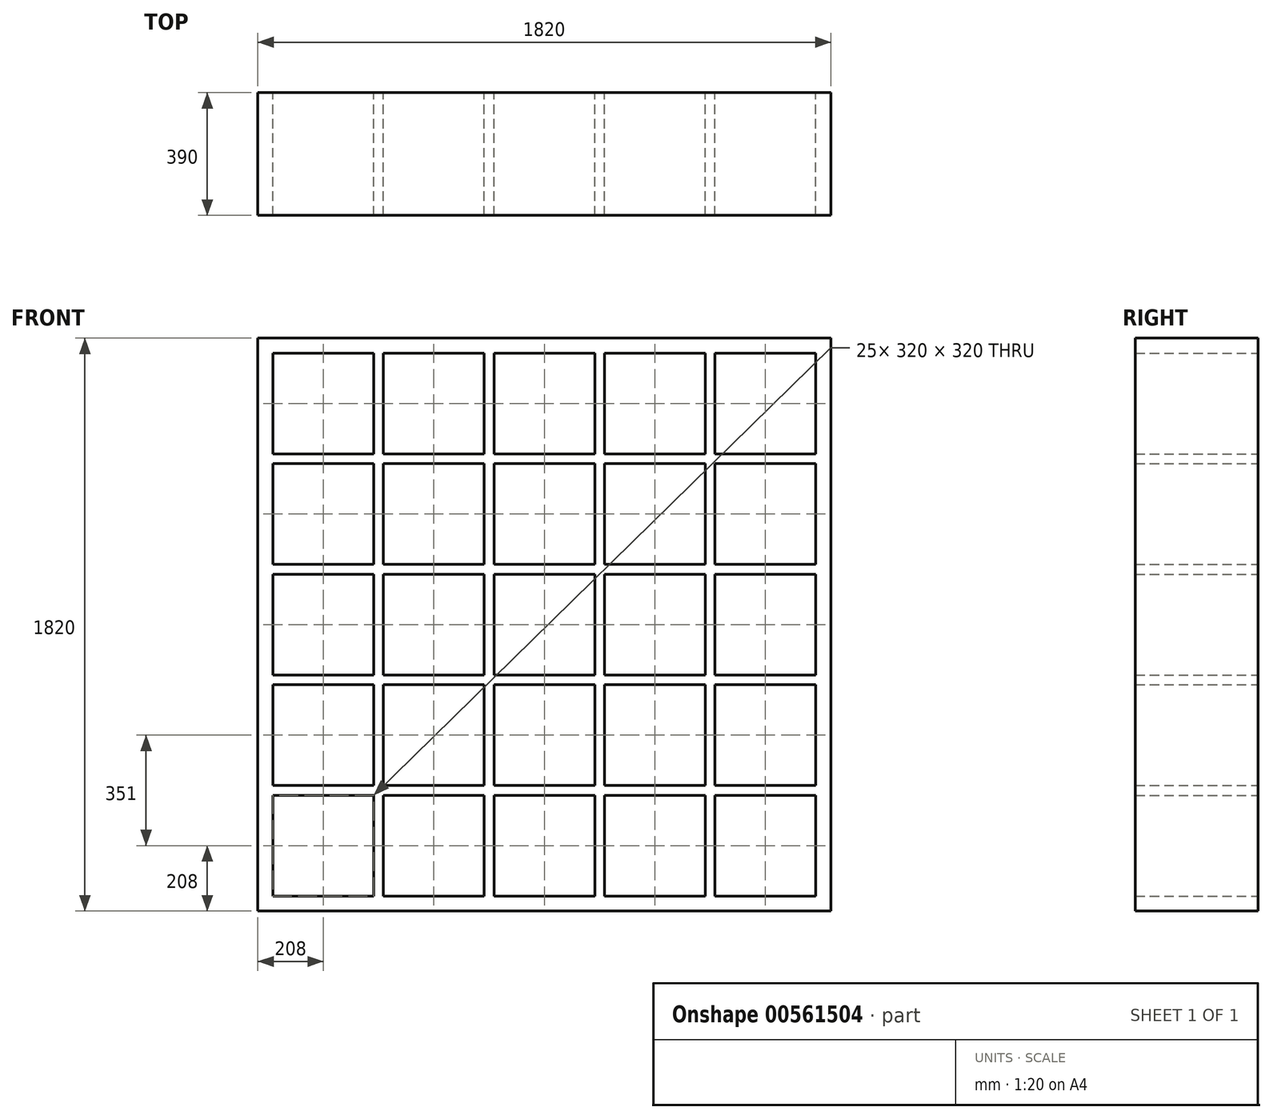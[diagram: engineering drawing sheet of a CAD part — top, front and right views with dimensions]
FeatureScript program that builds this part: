
annotation { "Feature Type Name" : "Feature", "Feature Type Description" : "" }
export const myFeature = defineFeature(function(context is Context, id is Id, definition is map)
    precondition{}
    {
        {
            var Q0;
            Q0=qCreatedBy(makeId("Front.planeOp"),FACE);
            var sketch = newSketch(context, id + "F0", { "sketchPlane" : qUnion([Q0])});
            skLineSegment(sketch, "E0.bottom", {"start": v(0, 0) * mm, "end": v(1820, 0) * mm});
            skLineSegment(sketch, "E0.top", {"start": v(0, 1820) * mm, "end": v(1820, 1820) * mm});
            skLineSegment(sketch, "E0.left", {"start": v(0, 0) * mm, "end": v(0, 1820) * mm});
            skLineSegment(sketch, "E0.right", {"start": v(1820, 0) * mm, "end": v(1820, 1820) * mm});
            skLineSegment(sketch, "E1.bottom", {"start": v(48, 368) * mm, "end": v(368, 368) * mm});
            skLineSegment(sketch, "E1.top", {"start": v(48, 48) * mm, "end": v(368, 48) * mm});
            skLineSegment(sketch, "E1.left", {"start": v(48, 368) * mm, "end": v(48, 48) * mm});
            skLineSegment(sketch, "E1.right", {"start": v(368, 368) * mm, "end": v(368, 48) * mm});
            skLineSegment(sketch, "E2.bottom", {"start": v(48, 719) * mm, "end": v(368, 719) * mm});
            skLineSegment(sketch, "E2.top", {"start": v(48, 399) * mm, "end": v(368, 399) * mm});
            skLineSegment(sketch, "E2.left", {"start": v(48, 719) * mm, "end": v(48, 399) * mm});
            skLineSegment(sketch, "E2.right", {"start": v(368, 719) * mm, "end": v(368, 399) * mm});
            skLineSegment(sketch, "E3.bottom", {"start": v(48, 1070) * mm, "end": v(368, 1070) * mm});
            skLineSegment(sketch, "E3.top", {"start": v(48, 750) * mm, "end": v(368, 750) * mm});
            skLineSegment(sketch, "E3.left", {"start": v(48, 1070) * mm, "end": v(48, 750) * mm});
            skLineSegment(sketch, "E3.right", {"start": v(368, 1070) * mm, "end": v(368, 750) * mm});
            skLineSegment(sketch, "E4.bottom", {"start": v(48, 1421) * mm, "end": v(368, 1421) * mm});
            skLineSegment(sketch, "E4.top", {"start": v(48, 1101) * mm, "end": v(368, 1101) * mm});
            skLineSegment(sketch, "E4.left", {"start": v(48, 1421) * mm, "end": v(48, 1101) * mm});
            skLineSegment(sketch, "E4.right", {"start": v(368, 1421) * mm, "end": v(368, 1101) * mm});
            skLineSegment(sketch, "E5.bottom", {"start": v(48, 1772) * mm, "end": v(368, 1772) * mm});
            skLineSegment(sketch, "E5.top", {"start": v(48, 1452) * mm, "end": v(368, 1452) * mm});
            skLineSegment(sketch, "E5.left", {"start": v(48, 1772) * mm, "end": v(48, 1452) * mm});
            skLineSegment(sketch, "E5.right", {"start": v(368, 1772) * mm, "end": v(368, 1452) * mm});
            skLineSegment(sketch, "E6.1.0.0", {"start": v(399, 1070) * mm, "end": v(719, 1070) * mm});
            skLineSegment(sketch, "E6.1.0.1", {"start": v(719, 719) * mm, "end": v(719, 399) * mm});
            skLineSegment(sketch, "E6.1.0.2", {"start": v(719, 1772) * mm, "end": v(719, 1452) * mm});
            skLineSegment(sketch, "E6.1.0.3", {"start": v(399, 1452) * mm, "end": v(719, 1452) * mm});
            skLineSegment(sketch, "E6.1.0.4", {"start": v(399, 719) * mm, "end": v(399, 399) * mm});
            skLineSegment(sketch, "E6.1.0.5", {"start": v(399, 399) * mm, "end": v(719, 399) * mm});
            skLineSegment(sketch, "E6.1.0.6", {"start": v(399, 719) * mm, "end": v(719, 719) * mm});
            skLineSegment(sketch, "E6.1.0.7", {"start": v(719, 368) * mm, "end": v(719, 48) * mm});
            skLineSegment(sketch, "E6.1.0.8", {"start": v(719, 1421) * mm, "end": v(719, 1101) * mm});
            skLineSegment(sketch, "E6.1.0.9", {"start": v(399, 48) * mm, "end": v(719, 48) * mm});
            skLineSegment(sketch, "E6.1.0.10", {"start": v(399, 750) * mm, "end": v(719, 750) * mm});
            skLineSegment(sketch, "E6.1.0.11", {"start": v(399, 1101) * mm, "end": v(719, 1101) * mm});
            skLineSegment(sketch, "E6.1.0.12", {"start": v(399, 1070) * mm, "end": v(399, 750) * mm});
            skLineSegment(sketch, "E6.1.0.13", {"start": v(719, 1070) * mm, "end": v(719, 750) * mm});
            skLineSegment(sketch, "E6.1.0.14", {"start": v(399, 368) * mm, "end": v(399, 48) * mm});
            skLineSegment(sketch, "E6.1.0.15", {"start": v(399, 368) * mm, "end": v(719, 368) * mm});
            skLineSegment(sketch, "E6.1.0.16", {"start": v(399, 1772) * mm, "end": v(399, 1452) * mm});
            skLineSegment(sketch, "E6.1.0.17", {"start": v(399, 1772) * mm, "end": v(719, 1772) * mm});
            skLineSegment(sketch, "E6.1.0.18", {"start": v(399, 1421) * mm, "end": v(399, 1101) * mm});
            skLineSegment(sketch, "E6.1.0.19", {"start": v(399, 1421) * mm, "end": v(719, 1421) * mm});
            skLineSegment(sketch, "E6.2.0.0", {"start": v(750, 1070) * mm, "end": v(1070, 1070) * mm});
            skLineSegment(sketch, "E6.2.0.1", {"start": v(1070, 719) * mm, "end": v(1070, 399) * mm});
            skLineSegment(sketch, "E6.2.0.2", {"start": v(1070, 1772) * mm, "end": v(1070, 1452) * mm});
            skLineSegment(sketch, "E6.2.0.3", {"start": v(750, 1452) * mm, "end": v(1070, 1452) * mm});
            skLineSegment(sketch, "E6.2.0.4", {"start": v(750, 719) * mm, "end": v(750, 399) * mm});
            skLineSegment(sketch, "E6.2.0.5", {"start": v(750, 399) * mm, "end": v(1070, 399) * mm});
            skLineSegment(sketch, "E6.2.0.6", {"start": v(750, 719) * mm, "end": v(1070, 719) * mm});
            skLineSegment(sketch, "E6.2.0.7", {"start": v(1070, 368) * mm, "end": v(1070, 48) * mm});
            skLineSegment(sketch, "E6.2.0.8", {"start": v(1070, 1421) * mm, "end": v(1070, 1101) * mm});
            skLineSegment(sketch, "E6.2.0.9", {"start": v(750, 48) * mm, "end": v(1070, 48) * mm});
            skLineSegment(sketch, "E6.2.0.10", {"start": v(750, 750) * mm, "end": v(1070, 750) * mm});
            skLineSegment(sketch, "E6.2.0.11", {"start": v(750, 1101) * mm, "end": v(1070, 1101) * mm});
            skLineSegment(sketch, "E6.2.0.12", {"start": v(750, 1070) * mm, "end": v(750, 750) * mm});
            skLineSegment(sketch, "E6.2.0.13", {"start": v(1070, 1070) * mm, "end": v(1070, 750) * mm});
            skLineSegment(sketch, "E6.2.0.14", {"start": v(750, 368) * mm, "end": v(750, 48) * mm});
            skLineSegment(sketch, "E6.2.0.15", {"start": v(750, 368) * mm, "end": v(1070, 368) * mm});
            skLineSegment(sketch, "E6.2.0.16", {"start": v(750, 1772) * mm, "end": v(750, 1452) * mm});
            skLineSegment(sketch, "E6.2.0.17", {"start": v(750, 1772) * mm, "end": v(1070, 1772) * mm});
            skLineSegment(sketch, "E6.2.0.18", {"start": v(750, 1421) * mm, "end": v(750, 1101) * mm});
            skLineSegment(sketch, "E6.2.0.19", {"start": v(750, 1421) * mm, "end": v(1070, 1421) * mm});
            skLineSegment(sketch, "E6.3.0.0", {"start": v(1101, 1070) * mm, "end": v(1421, 1070) * mm});
            skLineSegment(sketch, "E6.3.0.1", {"start": v(1421, 719) * mm, "end": v(1421, 399) * mm});
            skLineSegment(sketch, "E6.3.0.2", {"start": v(1421, 1772) * mm, "end": v(1421, 1452) * mm});
            skLineSegment(sketch, "E6.3.0.3", {"start": v(1101, 1452) * mm, "end": v(1421, 1452) * mm});
            skLineSegment(sketch, "E6.3.0.4", {"start": v(1101, 719) * mm, "end": v(1101, 399) * mm});
            skLineSegment(sketch, "E6.3.0.5", {"start": v(1101, 399) * mm, "end": v(1421, 399) * mm});
            skLineSegment(sketch, "E6.3.0.6", {"start": v(1101, 719) * mm, "end": v(1421, 719) * mm});
            skLineSegment(sketch, "E6.3.0.7", {"start": v(1421, 368) * mm, "end": v(1421, 48) * mm});
            skLineSegment(sketch, "E6.3.0.8", {"start": v(1421, 1421) * mm, "end": v(1421, 1101) * mm});
            skLineSegment(sketch, "E6.3.0.9", {"start": v(1101, 48) * mm, "end": v(1421, 48) * mm});
            skLineSegment(sketch, "E6.3.0.10", {"start": v(1101, 750) * mm, "end": v(1421, 750) * mm});
            skLineSegment(sketch, "E6.3.0.11", {"start": v(1101, 1101) * mm, "end": v(1421, 1101) * mm});
            skLineSegment(sketch, "E6.3.0.12", {"start": v(1101, 1070) * mm, "end": v(1101, 750) * mm});
            skLineSegment(sketch, "E6.3.0.13", {"start": v(1421, 1070) * mm, "end": v(1421, 750) * mm});
            skLineSegment(sketch, "E6.3.0.14", {"start": v(1101, 368) * mm, "end": v(1101, 48) * mm});
            skLineSegment(sketch, "E6.3.0.15", {"start": v(1101, 368) * mm, "end": v(1421, 368) * mm});
            skLineSegment(sketch, "E6.3.0.16", {"start": v(1101, 1772) * mm, "end": v(1101, 1452) * mm});
            skLineSegment(sketch, "E6.3.0.17", {"start": v(1101, 1772) * mm, "end": v(1421, 1772) * mm});
            skLineSegment(sketch, "E6.3.0.18", {"start": v(1101, 1421) * mm, "end": v(1101, 1101) * mm});
            skLineSegment(sketch, "E6.3.0.19", {"start": v(1101, 1421) * mm, "end": v(1421, 1421) * mm});
            skLineSegment(sketch, "E6.4.0.0", {"start": v(1452, 1070) * mm, "end": v(1772, 1070) * mm});
            skLineSegment(sketch, "E6.4.0.1", {"start": v(1772, 719) * mm, "end": v(1772, 399) * mm});
            skLineSegment(sketch, "E6.4.0.2", {"start": v(1772, 1772) * mm, "end": v(1772, 1452) * mm});
            skLineSegment(sketch, "E6.4.0.3", {"start": v(1452, 1452) * mm, "end": v(1772, 1452) * mm});
            skLineSegment(sketch, "E6.4.0.4", {"start": v(1452, 719) * mm, "end": v(1452, 399) * mm});
            skLineSegment(sketch, "E6.4.0.5", {"start": v(1452, 399) * mm, "end": v(1772, 399) * mm});
            skLineSegment(sketch, "E6.4.0.6", {"start": v(1452, 719) * mm, "end": v(1772, 719) * mm});
            skLineSegment(sketch, "E6.4.0.7", {"start": v(1772, 368) * mm, "end": v(1772, 48) * mm});
            skLineSegment(sketch, "E6.4.0.8", {"start": v(1772, 1421) * mm, "end": v(1772, 1101) * mm});
            skLineSegment(sketch, "E6.4.0.9", {"start": v(1452, 48) * mm, "end": v(1772, 48) * mm});
            skLineSegment(sketch, "E6.4.0.10", {"start": v(1452, 750) * mm, "end": v(1772, 750) * mm});
            skLineSegment(sketch, "E6.4.0.11", {"start": v(1452, 1101) * mm, "end": v(1772, 1101) * mm});
            skLineSegment(sketch, "E6.4.0.12", {"start": v(1452, 1070) * mm, "end": v(1452, 750) * mm});
            skLineSegment(sketch, "E6.4.0.13", {"start": v(1772, 1070) * mm, "end": v(1772, 750) * mm});
            skLineSegment(sketch, "E6.4.0.14", {"start": v(1452, 368) * mm, "end": v(1452, 48) * mm});
            skLineSegment(sketch, "E6.4.0.15", {"start": v(1452, 368) * mm, "end": v(1772, 368) * mm});
            skLineSegment(sketch, "E6.4.0.16", {"start": v(1452, 1772) * mm, "end": v(1452, 1452) * mm});
            skLineSegment(sketch, "E6.4.0.17", {"start": v(1452, 1772) * mm, "end": v(1772, 1772) * mm});
            skLineSegment(sketch, "E6.4.0.18", {"start": v(1452, 1421) * mm, "end": v(1452, 1101) * mm});
            skLineSegment(sketch, "E6.4.0.19", {"start": v(1452, 1421) * mm, "end": v(1772, 1421) * mm});
            skLineSegment(sketch, "E6.direction1", {"start": v(48, 48) * mm, "end": v(399, 48) * mm, "construction": true});
            skSolve(sketch);
        }
        {
            var Q0;
            Q0 = qSketchRegion(id + "F0", true);
            extrude(context, id + "F1", {"entities" : qUnion([Q0]), "depth" : 390 * mm, "offsetDistance" : 25 * mm, "symmetric" : true});
        }
    });
